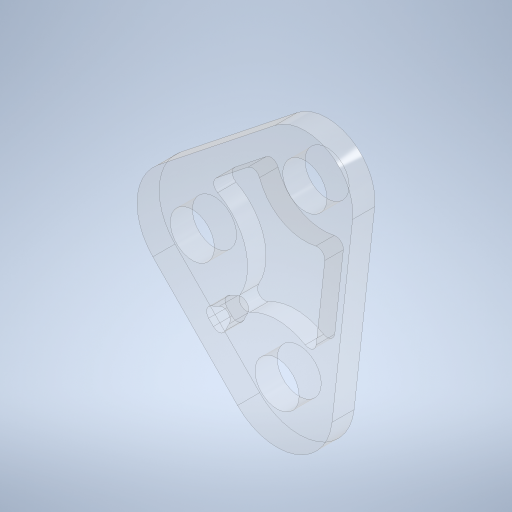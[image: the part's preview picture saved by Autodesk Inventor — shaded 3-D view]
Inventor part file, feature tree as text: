
AUTODESK INVENTOR PART (.ipt)
format: ipt  version: 2023 (Build 270158030, 158C)  size: 345,600 bytes
history: native  units: mm
features: sketch x3, extrude x3, projected_geometry x2, other x1, fillet x1
ambient origin geometry x8: Origin, YZ Plane, XZ Plane, XY Plane, X Axis, Y Axis, Z Axis, Center Point
bodies: Body1 (feature_tree)
feature tree (10):
  other  "ソリッド1"
  sketch  "スケッチ1"
  extrude  "押し出し1"  Depth=15.0mm
  extrude  "押し出し2"  Depth=3.0mm TaperAngle=0.0deg
  extrude  "押し出し3"  Depth=3.0mm
  fillet  "フィレット1"  Radius=2.5mm
  sketch  "スケッチ2"
  projected_geometry  "投影ループ1"
  sketch  "スケッチ3"
  projected_geometry  "投影ループ2"
